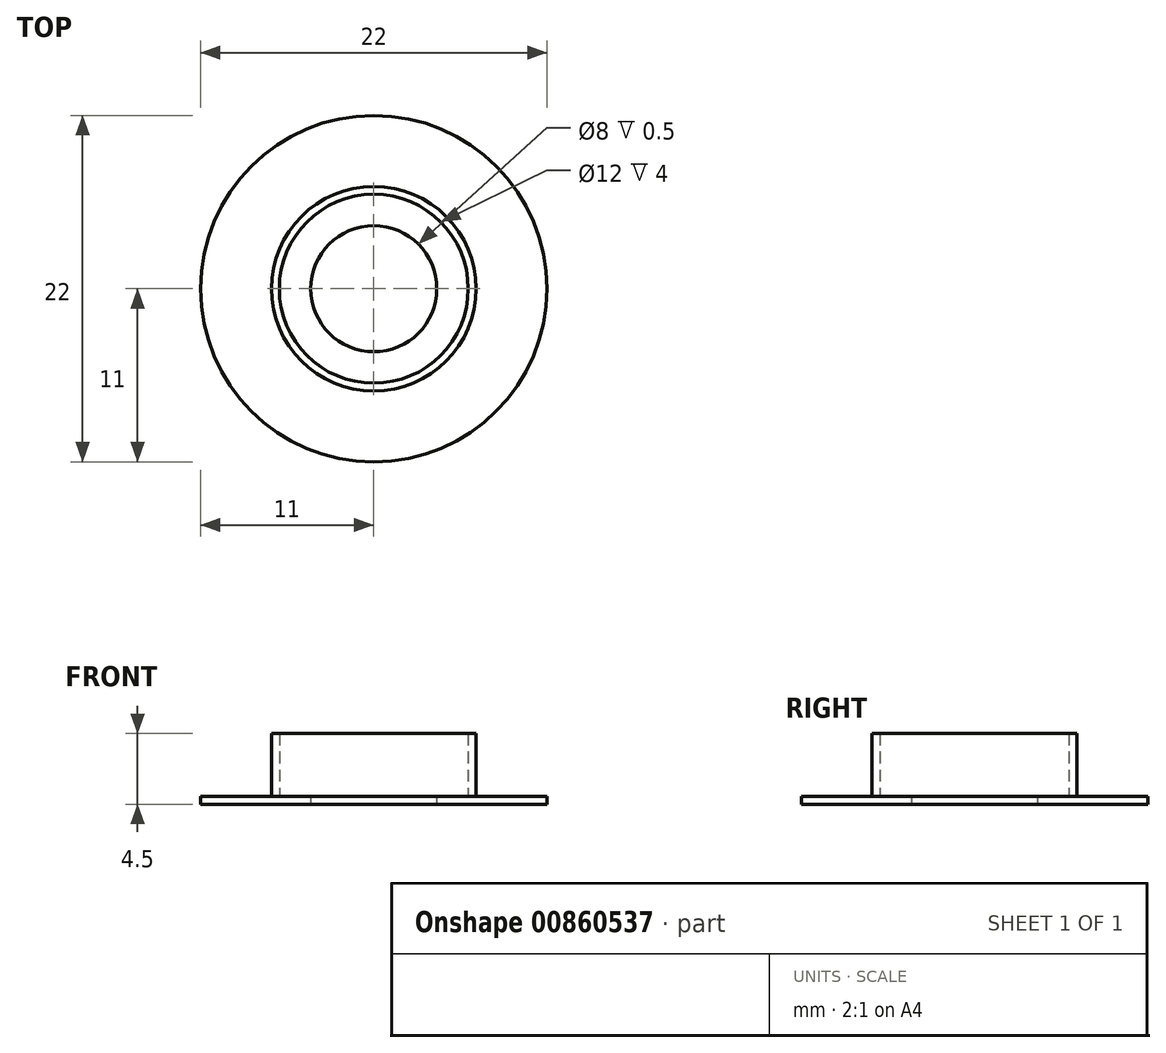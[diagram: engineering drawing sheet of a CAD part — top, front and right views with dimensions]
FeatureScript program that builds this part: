
annotation { "Feature Type Name" : "Feature", "Feature Type Description" : "" }
export const myFeature = defineFeature(function(context is Context, id is Id, definition is map)
    precondition{}
    {
        {
            var Q0;
            Q0=qCreatedBy(makeId("Top.planeOp"),FACE);
            var sketch = newSketch(context, id + "F0", { "sketchPlane" : qUnion([Q0])});
            skCircle(sketch, "E0", {"center": v(0, 0) * mm, "radius": 6.5 * mm});
            skCircle(sketch, "E1", {"center": v(0, 0) * mm, "radius": 6 * mm});
            skSolve(sketch);
        }
        {
            var Q0;
            Q0=qCreatedBy(makeId("Top.planeOp"),FACE);
            var sketch = newSketch(context, id + "F1", { "sketchPlane" : qUnion([Q0])});
            skCircle(sketch, "E2", {"center": v(0, 0) * mm, "radius": 4 * mm});
            skCircle(sketch, "E3", {"center": v(0, 0) * mm, "radius": 11 * mm});
            skSolve(sketch);
        }
        {
            var Q0;
            Q0 = qSketchRegion(id + "F1", true);
            extrude(context, id + "F2", {"entities" : qUnion([Q0]), "depth" : 0.5 * mm, "offsetDistance" : 25 * mm});
        }
        {
            var Q0;
            Q0 = qSketchRegion(id + "F0", true);
            extrude(context, id + "F3", {"entities" : qUnion([Q0]), "operationType" : NewBodyOperationType.ADD, "depth" : 4.5 * mm, "offsetDistance" : 25 * mm});
        }
    });
